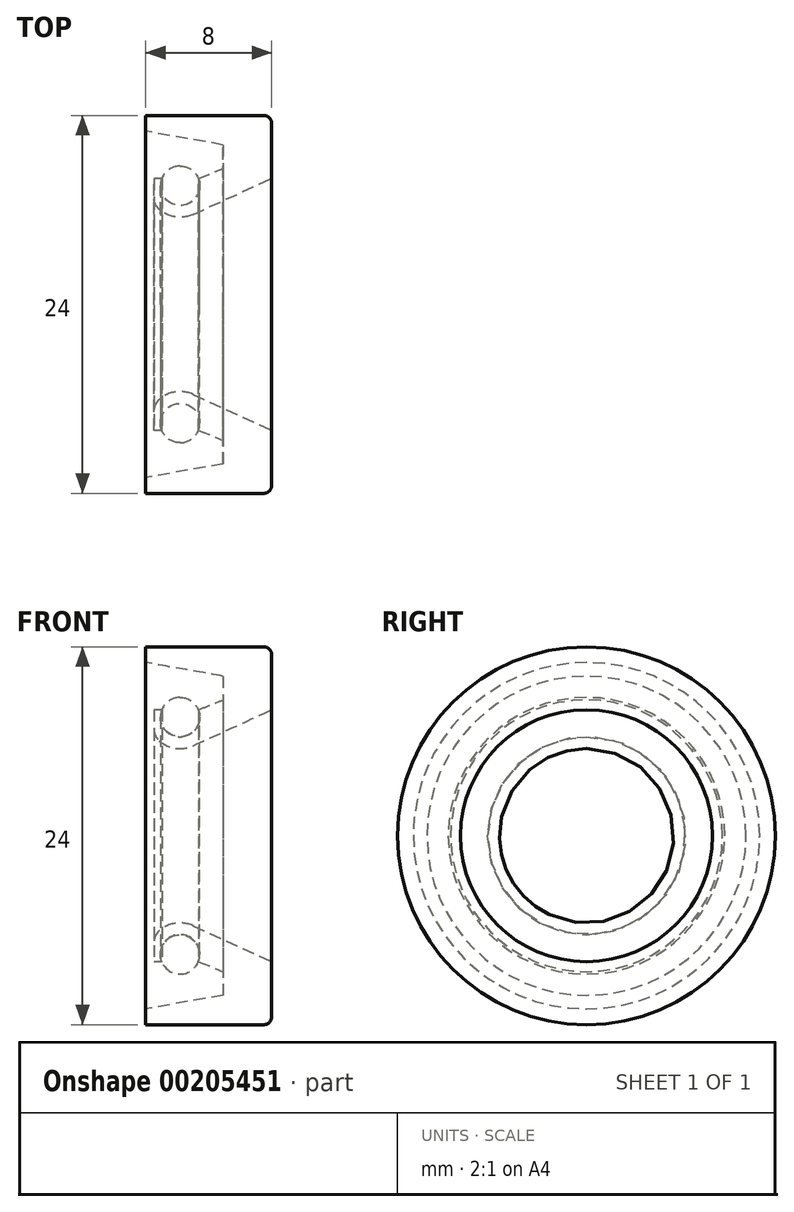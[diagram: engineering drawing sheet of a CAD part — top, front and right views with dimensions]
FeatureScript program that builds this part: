
annotation { "Feature Type Name" : "Feature", "Feature Type Description" : "" }
export const myFeature = defineFeature(function(context is Context, id is Id, definition is map)
    precondition{}
    {
        {
            var Q0;
            Q0=qCreatedBy(makeId("Front.planeOp"),FACE);
            var sketch = newSketch(context, id + "F0", { "sketchPlane" : qUnion([Q0])});
            skLineSegment(sketch, "E0", {"start": v(4, -2) * mm, "end": v(4, 1.5) * mm});
            skLineSegment(sketch, "E1", {"start": v(3.5, 2) * mm, "end": v(-4, 2) * mm});
            skLineSegment(sketch, "E2", {"start": v(-4, 2) * mm, "end": v(-4, 1) * mm});
            skLineSegment(sketch, "E3", {"start": v(-4, 1) * mm, "end": v(0.92, 0.13) * mm});
            skLineSegment(sketch, "E4", {"start": v(0.92, 0.13) * mm, "end": v(0.92, -1.37) * mm});
            skLineSegment(sketch, "E5", {"start": v(0.92, -1.37) * mm, "end": v(-0.65, -2) * mm});
            skArc(sketch, "E6", {"start": v(-2.98, -2) * mm, "mid": v(-1.81, -3.71) * mm, "end": v(-0.65, -2) * mm});
            skLineSegment(sketch, "E7", {"start": v(-2.98, -2) * mm, "end": v(-3.48, -2) * mm});
            skArc(sketch, "E8", {"start": v(-3.14, -3.97) * mm, "mid": v(-2.1, -4.44) * mm, "end": v(-0.98, -4.28) * mm});
            skLineSegment(sketch, "E9", {"start": v(4, -2) * mm, "end": v(-0.98, -4.28) * mm});
            skCircle(sketch, "E10", {"center": v(-1.81, -2.46) * mm, "radius": 1.25 * mm});
            skLineSegment(sketch, "E11", {"start": v(-3.48, -2) * mm, "end": v(-3.48, -3.22) * mm});
            skPoint(sketch, "E12.visualSharp", {"position": v(-3.48, -3.58) * mm});
            skArc(sketch, "E12.filletArc", {"start": v(-3.48, -3.22) * mm, "mid": v(-3.39, -3.63) * mm, "end": v(-3.14, -3.97) * mm});
            skPoint(sketch, "E13.visualSharp", {"position": v(4, 2) * mm});
            skArc(sketch, "E13.filletArc", {"start": v(4, 1.5) * mm, "mid": v(3.85, 1.85) * mm, "end": v(3.5, 2) * mm});
            skLineSegment(sketch, "E14", {"start": v(-4.46, -10) * mm, "end": v(5.89, -10) * mm, "construction": true});
            skLineSegment(sketch, "E15", {"start": v(-0.65, -2) * mm, "end": v(-2.78, -2.85) * mm, "construction": true});
            skSolve(sketch);
        }
        {
            var Q0;
            Q0=makeQuery(id+"F0.imprint","IMPRINT",FACE,{"disambiguationData":[TD([[makeQuery(id+"F0.imprint","IMPRINT",EDGE,{"derivedFrom":sQuery(id+"F0.wireOp",EDGE,"E0")}),1.0]])]});
            var Q1;
            Q1=sQuery(id+"F0.wireOp",EDGE,"E14");
            revolve(context, id + "F1", {"entities" : qUnion([Q0]), "axis" : qUnion([Q1]), "revolveType" : RevolveType.FULL});
        }
        {
            var Q0;
            Q0=qCreatedBy(makeId("Front.planeOp"),FACE);
            var sketch = newSketch(context, id + "F2", { "sketchPlane" : qUnion([Q0])});
            skCircle(sketch, "E16.0", {"center": v(-1.81, -2.46) * mm, "radius": 1.25 * mm});
            skSolve(sketch);
        }
        {
            var Q0;
            Q0=makeQuery(id+"F2.imprint","IMPRINT",FACE,{"disambiguationData":[TD([[makeQuery(id+"F2.imprint","IMPRINT",EDGE,{"derivedFrom":sQuery(id+"F2.wireOp",EDGE,"E16.0")}),1.0]])]});
            var Q1;
            Q1=makeQuery(id+"F1.opRevolve","SWEPT_EDGE",EDGE,{"disambiguationData":[OSD([sQuery(id+"F0.wireOp",EDGE,"E7"),sQuery(id+"F0.wireOp",EDGE,"E11")])]});
            revolve(context, id + "F3", {"entities" : qUnion([Q0]), "axis" : qUnion([Q1]), "revolveType" : RevolveType.FULL});
        }
    });
